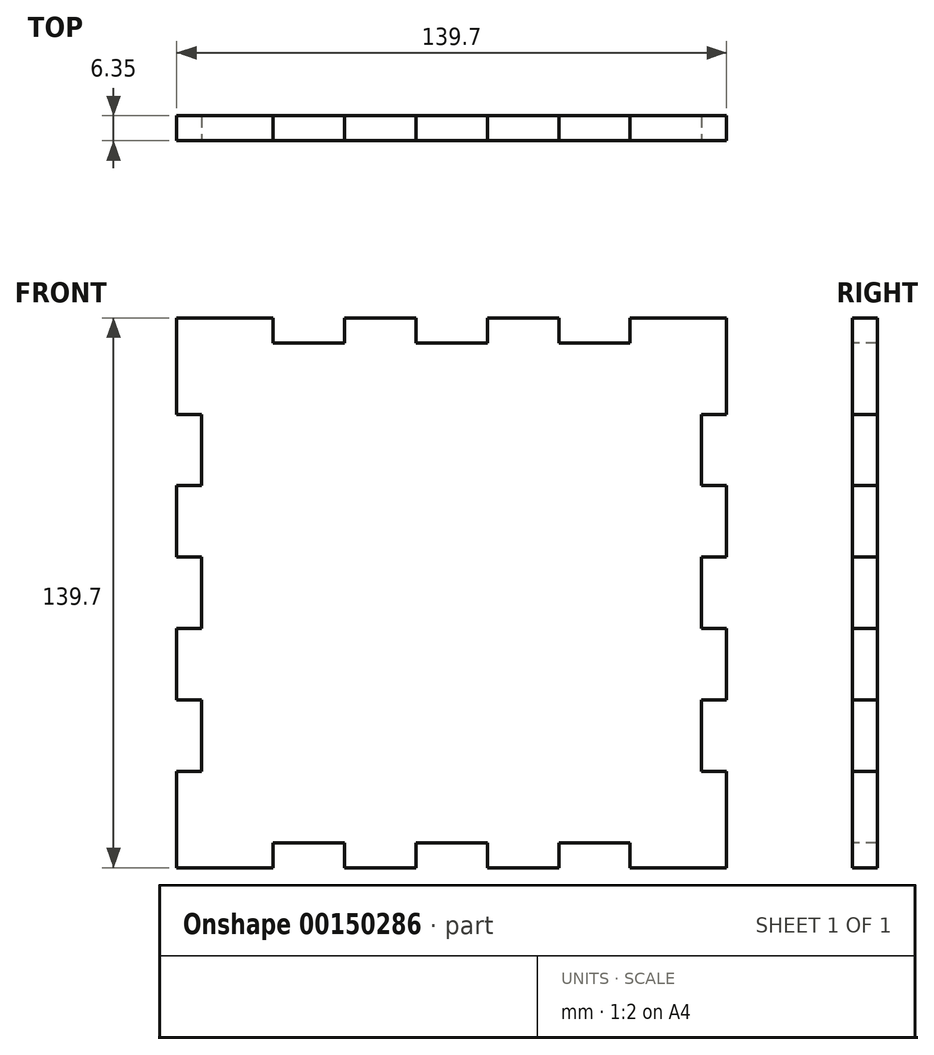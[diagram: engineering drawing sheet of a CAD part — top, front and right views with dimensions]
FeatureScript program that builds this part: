
annotation { "Feature Type Name" : "Feature", "Feature Type Description" : "" }
export const myFeature = defineFeature(function(context is Context, id is Id, definition is map)
    precondition{}
    {
        {
            var Q0;
            Q0=qCreatedBy(makeId("Front.planeOp"),FACE);
            var sketch = newSketch(context, id + "F0", { "sketchPlane" : qUnion([Q0])});
            skLineSegment(sketch, "E0.bottom", {"start": v(-69.85, 69.85) * mm, "end": v(69.85, 69.85) * mm});
            skLineSegment(sketch, "E0.top", {"start": v(-69.85, -69.85) * mm, "end": v(69.85, -69.85) * mm});
            skLineSegment(sketch, "E0.left", {"start": v(-69.85, 69.85) * mm, "end": v(-69.85, -69.85) * mm});
            skLineSegment(sketch, "E0.right", {"start": v(69.85, 69.85) * mm, "end": v(69.85, -69.85) * mm});
            skSolve(sketch);
        }
        {
            var Q0;
            Q0 = qSketchRegion(id + "F0", true);
            extrude(context, id + "F1", {"entities" : qUnion([Q0]), "depth" : 6.35 * mm});
        }
        {
            var Q0;
            Q0=makeQuery(id+"F1.opExtrude","CAP_FACE",FACE,{"disambiguationData":[OSD([sQuery(id+"F0.wireOp",EDGE,"E0.bottom"),sQuery(id+"F0.wireOp",EDGE,"E0.top"),sQuery(id+"F0.wireOp",EDGE,"E0.left"),sQuery(id+"F0.wireOp",EDGE,"E0.right")])],"isStart":false});
            var sketch = newSketch(context, id + "F2", { "sketchPlane" : qUnion([Q0])});
            skLineSegment(sketch, "E1.bottom", {"start": v(-69.85, 69.85) * mm, "end": v(69.85, 69.85) * mm});
            skLineSegment(sketch, "E1.top", {"start": v(-69.85, 63.5) * mm, "end": v(69.85, 63.5) * mm});
            skLineSegment(sketch, "E1.left", {"start": v(-69.85, 69.85) * mm, "end": v(-69.85, 63.5) * mm});
            skLineSegment(sketch, "E1.right", {"start": v(69.85, 69.85) * mm, "end": v(69.85, 63.5) * mm});
            skLineSegment(sketch, "E2.bottom", {"start": v(69.85, 69.85) * mm, "end": v(63.5, 69.85) * mm});
            skLineSegment(sketch, "E2.top", {"start": v(69.85, -69.85) * mm, "end": v(63.5, -69.85) * mm});
            skLineSegment(sketch, "E2.left", {"start": v(69.85, 69.85) * mm, "end": v(69.85, -69.85) * mm});
            skLineSegment(sketch, "E2.right", {"start": v(63.5, 69.85) * mm, "end": v(63.5, -69.85) * mm});
            skLineSegment(sketch, "E3.bottom", {"start": v(69.85, -69.85) * mm, "end": v(-69.85, -69.85) * mm});
            skLineSegment(sketch, "E3.top", {"start": v(69.85, -63.5) * mm, "end": v(-69.85, -63.5) * mm});
            skLineSegment(sketch, "E3.left", {"start": v(69.85, -69.85) * mm, "end": v(69.85, -63.5) * mm});
            skLineSegment(sketch, "E3.right", {"start": v(-69.85, -69.85) * mm, "end": v(-69.85, -63.5) * mm});
            skLineSegment(sketch, "E4.bottom", {"start": v(-69.85, -69.85) * mm, "end": v(-63.5, -69.85) * mm});
            skLineSegment(sketch, "E4.top", {"start": v(-69.85, 69.85) * mm, "end": v(-63.5, 69.85) * mm});
            skLineSegment(sketch, "E4.left", {"start": v(-69.85, -69.85) * mm, "end": v(-69.85, 69.85) * mm});
            skLineSegment(sketch, "E4.right", {"start": v(-63.5, -69.85) * mm, "end": v(-63.5, 69.85) * mm});
            skLineSegment(sketch, "E5", {"start": v(-45.36, 69.85) * mm, "end": v(-45.36, -69.85) * mm});
            skLineSegment(sketch, "E6", {"start": v(-27.21, 69.85) * mm, "end": v(-27.21, -69.85) * mm});
            skLineSegment(sketch, "E7", {"start": v(-9.07, 69.85) * mm, "end": v(-9.07, -69.85) * mm});
            skLineSegment(sketch, "E8", {"start": v(9.07, 69.85) * mm, "end": v(9.07, -69.85) * mm});
            skLineSegment(sketch, "E9", {"start": v(27.21, 69.85) * mm, "end": v(27.21, -69.85) * mm});
            skLineSegment(sketch, "E10", {"start": v(45.36, 69.85) * mm, "end": v(45.36, -69.85) * mm});
            skLineSegment(sketch, "E11", {"start": v(-69.85, 45.36) * mm, "end": v(69.85, 45.36) * mm});
            skLineSegment(sketch, "E12", {"start": v(-69.85, 27.21) * mm, "end": v(69.85, 27.21) * mm});
            skLineSegment(sketch, "E13", {"start": v(-69.85, 9.07) * mm, "end": v(69.85, 9.07) * mm});
            skLineSegment(sketch, "E14", {"start": v(-69.85, -9.07) * mm, "end": v(69.85, -9.07) * mm});
            skLineSegment(sketch, "E15", {"start": v(-69.85, -27.21) * mm, "end": v(69.85, -27.21) * mm});
            skLineSegment(sketch, "E16", {"start": v(-69.85, -45.36) * mm, "end": v(69.85, -45.36) * mm});
            skSolve(sketch);
        }
        {
            var Q0;
            {var subQ5=sQuery(id+"F2.wireOp",EDGE,"E4.top");Q0=makeQuery(id+"F2.imprint","IMPRINT",FACE,{"disambiguationData":[TD([[makeQuery(id+"F2.imprint","IMPRINT",EDGE,{"derivedFrom":subQ5}),-1.0]])]});}
            var Q1;
            {var subQ0=sQuery(id+"F2.wireOp",EDGE,"E5");var subQ1=sQuery(id+"F2.wireOp",EDGE,"E1.bottom");var subQ2=makeQuery(id+"F2.imprint","INTERSECT",VERTEX,{"derivedFrom":[subQ1,subQ0]});Q1=makeQuery(id+"F2.imprint","IMPRINT",FACE,{"disambiguationData":[TD([[makeQuery(id+"F2.imprint","IMPRINT",EDGE,{"disambiguationData":[TD([[subQ2,-1.0]])],"derivedFrom":subQ1}),-1.0]])]});}
            var Q2;
            {var subQ0=sQuery(id+"F2.wireOp",EDGE,"E7");var subQ1=sQuery(id+"F2.wireOp",EDGE,"E1.bottom");var subQ2=makeQuery(id+"F2.imprint","INTERSECT",VERTEX,{"derivedFrom":[subQ1,subQ0]});Q2=makeQuery(id+"F2.imprint","IMPRINT",FACE,{"disambiguationData":[TD([[makeQuery(id+"F2.imprint","IMPRINT",EDGE,{"disambiguationData":[TD([[subQ2,-1.0]])],"derivedFrom":subQ1}),-1.0]])]});}
            var Q3;
            {var subQ0=sQuery(id+"F2.wireOp",EDGE,"E9");var subQ1=sQuery(id+"F2.wireOp",EDGE,"E1.bottom");var subQ2=makeQuery(id+"F2.imprint","INTERSECT",VERTEX,{"derivedFrom":[subQ1,subQ0]});Q3=makeQuery(id+"F2.imprint","IMPRINT",FACE,{"disambiguationData":[TD([[makeQuery(id+"F2.imprint","IMPRINT",EDGE,{"disambiguationData":[TD([[subQ2,-1.0]])],"derivedFrom":subQ1}),-1.0]])]});}
            var Q4;
            {var subQ5=sQuery(id+"F2.wireOp",EDGE,"E2.bottom");Q4=makeQuery(id+"F2.imprint","IMPRINT",FACE,{"disambiguationData":[TD([[makeQuery(id+"F2.imprint","IMPRINT",EDGE,{"derivedFrom":subQ5}),-1.0]])]});}
            var Q5;
            {var subQ0=sQuery(id+"F2.wireOp",EDGE,"E11");var subQ1=sQuery(id+"F2.wireOp",EDGE,"E2.left");var subQ2=makeQuery(id+"F2.imprint","INTERSECT",VERTEX,{"derivedFrom":[subQ1,subQ0]});Q5=makeQuery(id+"F2.imprint","IMPRINT",FACE,{"disambiguationData":[TD([[makeQuery(id+"F2.imprint","IMPRINT",EDGE,{"disambiguationData":[TD([[subQ2,-1.0]])],"derivedFrom":subQ1}),-1.0]])]});}
            var Q6;
            {var subQ0=sQuery(id+"F2.wireOp",EDGE,"E13");var subQ1=sQuery(id+"F2.wireOp",EDGE,"E2.left");var subQ2=makeQuery(id+"F2.imprint","INTERSECT",VERTEX,{"derivedFrom":[subQ1,subQ0]});Q6=makeQuery(id+"F2.imprint","IMPRINT",FACE,{"disambiguationData":[TD([[makeQuery(id+"F2.imprint","IMPRINT",EDGE,{"disambiguationData":[TD([[subQ2,-1.0]])],"derivedFrom":subQ1}),-1.0]])]});}
            var Q7;
            {var subQ0=sQuery(id+"F2.wireOp",EDGE,"E15");var subQ1=sQuery(id+"F2.wireOp",EDGE,"E2.left");var subQ2=makeQuery(id+"F2.imprint","INTERSECT",VERTEX,{"derivedFrom":[subQ1,subQ0]});Q7=makeQuery(id+"F2.imprint","IMPRINT",FACE,{"disambiguationData":[TD([[makeQuery(id+"F2.imprint","IMPRINT",EDGE,{"disambiguationData":[TD([[subQ2,-1.0]])],"derivedFrom":subQ1}),-1.0]])]});}
            var Q8;
            {var subQ5=sQuery(id+"F2.wireOp",EDGE,"E3.left");Q8=makeQuery(id+"F2.imprint","IMPRINT",FACE,{"disambiguationData":[TD([[makeQuery(id+"F2.imprint","IMPRINT",EDGE,{"derivedFrom":subQ5}),-1.0]])]});}
            var Q9;
            {var subQ0=sQuery(id+"F2.wireOp",EDGE,"E9");var subQ1=sQuery(id+"F2.wireOp",EDGE,"E3.bottom");var subQ2=makeQuery(id+"F2.imprint","INTERSECT",VERTEX,{"derivedFrom":[subQ1,subQ0]});Q9=makeQuery(id+"F2.imprint","IMPRINT",FACE,{"disambiguationData":[TD([[makeQuery(id+"F2.imprint","IMPRINT",EDGE,{"disambiguationData":[TD([[subQ2,-1.0]])],"derivedFrom":subQ1}),1.0]])]});}
            var Q10;
            {var subQ0=sQuery(id+"F2.wireOp",EDGE,"E7");var subQ1=sQuery(id+"F2.wireOp",EDGE,"E3.bottom");var subQ2=makeQuery(id+"F2.imprint","INTERSECT",VERTEX,{"derivedFrom":[subQ1,subQ0]});Q10=makeQuery(id+"F2.imprint","IMPRINT",FACE,{"disambiguationData":[TD([[makeQuery(id+"F2.imprint","IMPRINT",EDGE,{"disambiguationData":[TD([[subQ2,-1.0]])],"derivedFrom":subQ1}),1.0]])]});}
            var Q11;
            {var subQ0=sQuery(id+"F2.wireOp",EDGE,"E5");var subQ1=sQuery(id+"F2.wireOp",EDGE,"E3.bottom");var subQ2=makeQuery(id+"F2.imprint","INTERSECT",VERTEX,{"derivedFrom":[subQ1,subQ0]});Q11=makeQuery(id+"F2.imprint","IMPRINT",FACE,{"disambiguationData":[TD([[makeQuery(id+"F2.imprint","IMPRINT",EDGE,{"disambiguationData":[TD([[subQ2,-1.0]])],"derivedFrom":subQ1}),1.0]])]});}
            var Q12;
            {var subQ5=sQuery(id+"F2.wireOp",EDGE,"E4.bottom");Q12=makeQuery(id+"F2.imprint","IMPRINT",FACE,{"disambiguationData":[TD([[makeQuery(id+"F2.imprint","IMPRINT",EDGE,{"derivedFrom":subQ5}),1.0]])]});}
            var Q13;
            {var subQ0=sQuery(id+"F2.wireOp",EDGE,"E15");var subQ1=sQuery(id+"F2.wireOp",EDGE,"E4.left");var subQ2=makeQuery(id+"F2.imprint","INTERSECT",VERTEX,{"derivedFrom":[subQ1,subQ0]});Q13=makeQuery(id+"F2.imprint","IMPRINT",FACE,{"disambiguationData":[TD([[makeQuery(id+"F2.imprint","IMPRINT",EDGE,{"disambiguationData":[TD([[subQ2,-1.0]])],"derivedFrom":subQ1}),1.0]])]});}
            var Q14;
            {var subQ0=sQuery(id+"F2.wireOp",EDGE,"E13");var subQ1=sQuery(id+"F2.wireOp",EDGE,"E4.left");var subQ2=makeQuery(id+"F2.imprint","INTERSECT",VERTEX,{"derivedFrom":[subQ1,subQ0]});Q14=makeQuery(id+"F2.imprint","IMPRINT",FACE,{"disambiguationData":[TD([[makeQuery(id+"F2.imprint","IMPRINT",EDGE,{"disambiguationData":[TD([[subQ2,-1.0]])],"derivedFrom":subQ1}),1.0]])]});}
            var Q15;
            {var subQ0=sQuery(id+"F2.wireOp",EDGE,"E11");var subQ1=sQuery(id+"F2.wireOp",EDGE,"E4.left");var subQ2=makeQuery(id+"F2.imprint","INTERSECT",VERTEX,{"derivedFrom":[subQ1,subQ0]});Q15=makeQuery(id+"F2.imprint","IMPRINT",FACE,{"disambiguationData":[TD([[makeQuery(id+"F2.imprint","IMPRINT",EDGE,{"disambiguationData":[TD([[subQ2,-1.0]])],"derivedFrom":subQ1}),1.0]])]});}
            extrude(context, id + "F3", {"entities" : qUnion([Q0, Q1, Q2, Q3, Q4, Q5, Q6, Q7, Q8, Q9, Q10, Q11, Q12, Q13, Q14, Q15]), "operationType" : NewBodyOperationType.REMOVE, "oppositeDirection" : true, "depth" : 25.4 * mm});
        }
    });
